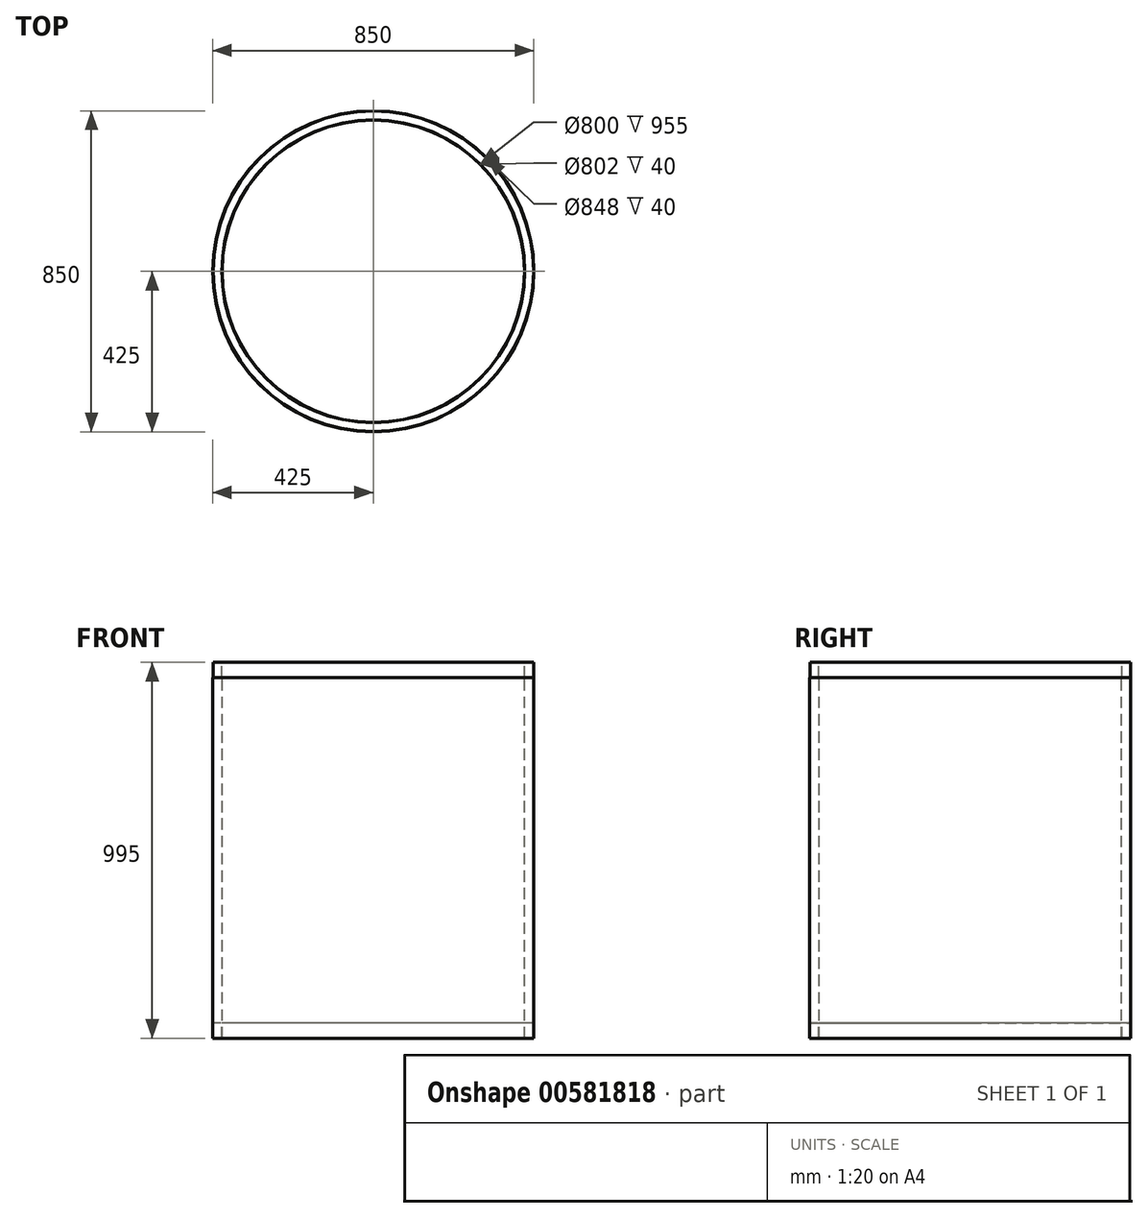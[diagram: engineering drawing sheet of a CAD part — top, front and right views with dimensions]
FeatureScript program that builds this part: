
annotation { "Feature Type Name" : "Feature", "Feature Type Description" : "" }
export const myFeature = defineFeature(function(context is Context, id is Id, definition is map)
    precondition{}
    {
        {
            var Q0;
            Q0=qCreatedBy(makeId("Front.planeOp"),FACE);
            var sketch = newSketch(context, id + "F0", { "sketchPlane" : qUnion([Q0])});
            skLineSegment(sketch, "E0", {"start": v(0, 345.75) * mm, "end": v(0, -558.03) * mm, "construction": true});
            skLineSegment(sketch, "E1", {"start": v(-400, -518.84) * mm, "end": v(-400, 436.16) * mm});
            skLineSegment(sketch, "E2", {"start": v(-400, 436.16) * mm, "end": v(-401, 436.16) * mm});
            skLineSegment(sketch, "E3", {"start": v(-401, 436.16) * mm, "end": v(-401, 476.16) * mm});
            skLineSegment(sketch, "E4", {"start": v(-401, 476.16) * mm, "end": v(-424, 476.16) * mm});
            skLineSegment(sketch, "E5", {"start": v(-424, 476.16) * mm, "end": v(-424, 436.16) * mm});
            skLineSegment(sketch, "E6", {"start": v(-424, 436.16) * mm, "end": v(-425, 436.16) * mm});
            skLineSegment(sketch, "E7", {"start": v(-425, 436.16) * mm, "end": v(-425, -518.84) * mm});
            skLineSegment(sketch, "E8", {"start": v(-425, -518.84) * mm, "end": v(-424, -518.84) * mm});
            skLineSegment(sketch, "E9", {"start": v(-424, -518.84) * mm, "end": v(-424, -478.84) * mm});
            skLineSegment(sketch, "E10", {"start": v(-424, -478.84) * mm, "end": v(-401, -478.84) * mm});
            skLineSegment(sketch, "E11", {"start": v(-401, -478.84) * mm, "end": v(-401, -518.84) * mm});
            skLineSegment(sketch, "E12", {"start": v(-401, -518.84) * mm, "end": v(-400, -518.84) * mm});
            skSolve(sketch);
        }
        {
            var Q0;
            Q0 = qSketchRegion(id + "F0", true);
            var Q1;
            Q1=sQuery(id+"F0.wireOp",EDGE,"E0");
            revolve(context, id + "F1", {"entities" : qUnion([Q0]), "axis" : qUnion([Q1]), "revolveType" : RevolveType.FULL});
        }
    });
